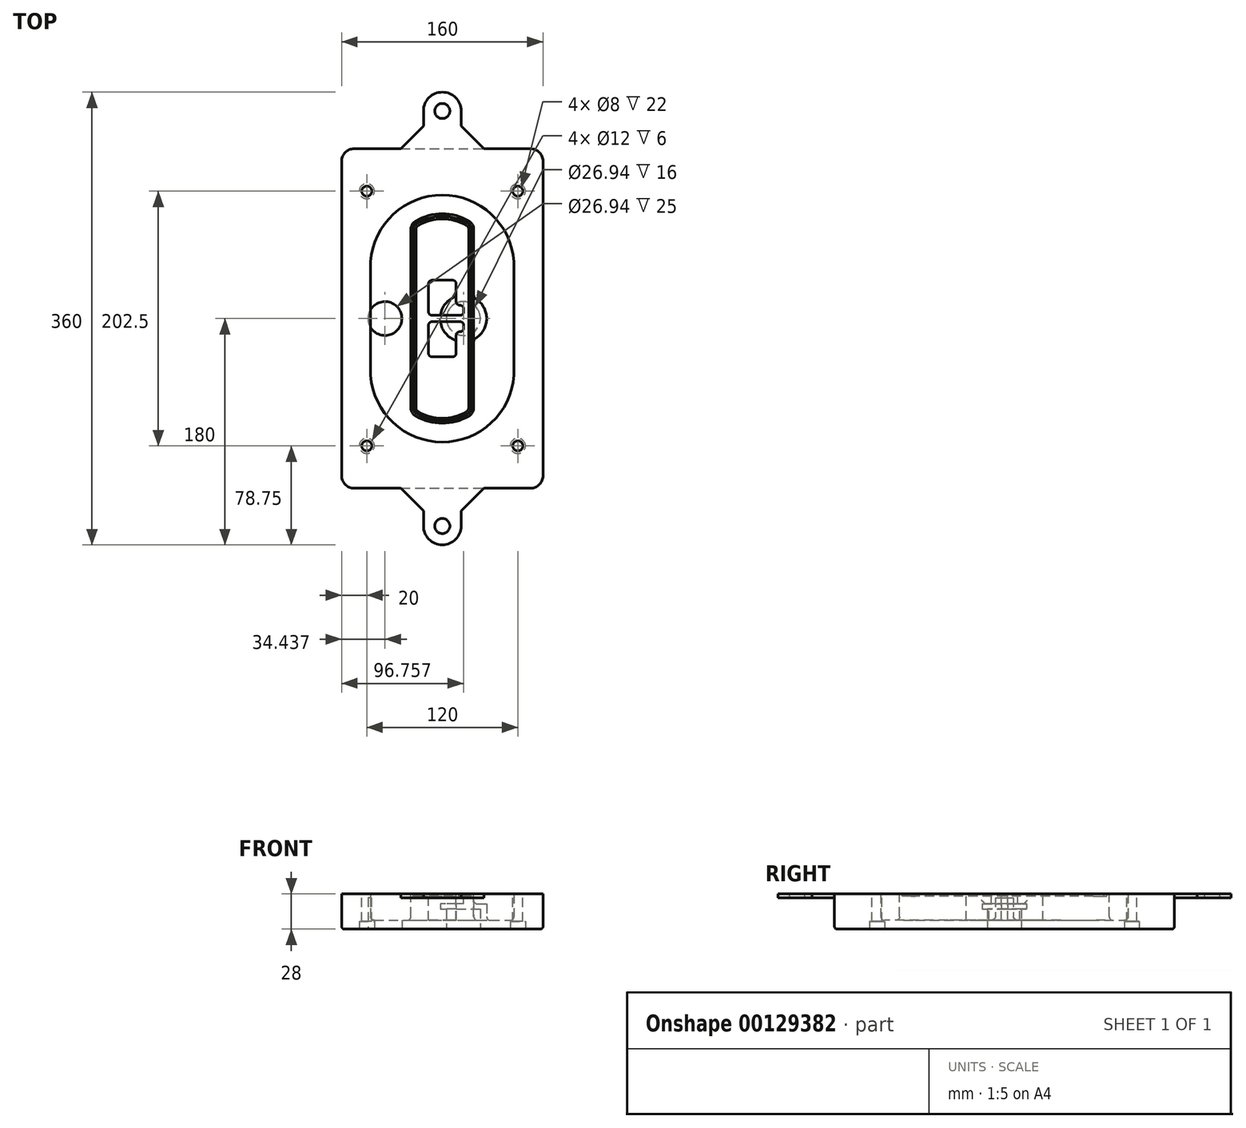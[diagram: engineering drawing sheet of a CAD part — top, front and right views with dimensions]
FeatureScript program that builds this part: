
annotation { "Feature Type Name" : "Feature", "Feature Type Description" : "" }
export const myFeature = defineFeature(function(context is Context, id is Id, definition is map)
    precondition{}
    {
        {
            var Q0;
            Q0=qCreatedBy(makeId("Top.planeOp"),FACE);
            var sketch = newSketch(context, id + "F0", { "sketchPlane" : qUnion([Q0])});
            skPoint(sketch, "E0.rect.middle", {"position": v(0, 0) * mm});
            skLineSegment(sketch, "E1.bottom", {"start": v(-70, -135) * mm, "end": v(70, -135) * mm});
            skLineSegment(sketch, "E1.top", {"start": v(-70, 135) * mm, "end": v(70, 135) * mm});
            skLineSegment(sketch, "E1.left", {"start": v(-80, -125) * mm, "end": v(-80, 125) * mm});
            skLineSegment(sketch, "E1.right", {"start": v(80, -125) * mm, "end": v(80, 125) * mm});
            skLineSegment(sketch, "E2", {"start": v(-80, 135) * mm, "end": v(80, -135) * mm, "construction": true});
            skLineSegment(sketch, "E3", {"start": v(80, 135) * mm, "end": v(-80, -135) * mm, "construction": true});
            skCircle(sketch, "E4", {"center": v(-60, 101.25) * mm, "radius": 4 * mm});
            skCircle(sketch, "E5", {"center": v(60, 101.25) * mm, "radius": 4 * mm});
            skCircle(sketch, "E6", {"center": v(60, -101.25) * mm, "radius": 4 * mm});
            skCircle(sketch, "E7", {"center": v(-60, -101.25) * mm, "radius": 4 * mm});
            skLineSegment(sketch, "E8", {"start": v(-60, 101.25) * mm, "end": v(60, 101.25) * mm, "construction": true});
            skLineSegment(sketch, "E9", {"start": v(60, 101.25) * mm, "end": v(60, -101.25) * mm, "construction": true});
            skLineSegment(sketch, "E10", {"start": v(60, -101.25) * mm, "end": v(-60, -101.25) * mm, "construction": true});
            skLineSegment(sketch, "E11", {"start": v(-60, -101.25) * mm, "end": v(-60, 101.25) * mm, "construction": true});
            skLineSegment(sketch, "E12", {"start": v(-60, 44.66) * mm, "end": v(-60, -44.66) * mm});
            skLineSegment(sketch, "E13", {"start": v(60, 44.66) * mm, "end": v(60, -44.66) * mm});
            skArc(sketch, "E14", {"start": v(59.98, 45.37) * mm, "mid": v(0, 101.25) * mm, "end": v(-59.98, 45.37) * mm});
            skArc(sketch, "E15", {"start": v(-59.98, -45.37) * mm, "mid": v(0, -101.25) * mm, "end": v(59.98, -45.37) * mm});
            skLineSegment(sketch, "E16", {"start": v(-60, 0) * mm, "end": v(60, 0) * mm, "construction": true});
            skPoint(sketch, "E17.visualSharp", {"position": v(-60, -45) * mm});
            skArc(sketch, "E17.filletArc", {"start": v(-60, -44.66) * mm, "mid": v(-60, -45.02) * mm, "end": v(-59.98, -45.37) * mm});
            skPoint(sketch, "E18.visualSharp", {"position": v(-60, 45) * mm});
            skArc(sketch, "E18.filletArc", {"start": v(-59.98, 45.37) * mm, "mid": v(-60, 45.02) * mm, "end": v(-60, 44.66) * mm});
            skPoint(sketch, "E19.visualSharp", {"position": v(60, 45) * mm});
            skArc(sketch, "E19.filletArc", {"start": v(60, 44.66) * mm, "mid": v(60, 45.02) * mm, "end": v(59.98, 45.37) * mm});
            skPoint(sketch, "E20.visualSharp", {"position": v(60, -45) * mm});
            skArc(sketch, "E20.filletArc", {"start": v(59.98, -45.37) * mm, "mid": v(60, -45.02) * mm, "end": v(60, -44.66) * mm});
            skPoint(sketch, "E21.visualSharp", {"position": v(-80, 135) * mm});
            skArc(sketch, "E21.filletArc", {"start": v(-70, 135) * mm, "mid": v(-77.07, 132.07) * mm, "end": v(-80, 125) * mm});
            skPoint(sketch, "E22.visualSharp", {"position": v(80, 135) * mm});
            skArc(sketch, "E22.filletArc", {"start": v(80, 125) * mm, "mid": v(77.07, 132.07) * mm, "end": v(70, 135) * mm});
            skPoint(sketch, "E23.visualSharp", {"position": v(80, -135) * mm});
            skArc(sketch, "E23.filletArc", {"start": v(70, -135) * mm, "mid": v(77.07, -132.07) * mm, "end": v(80, -125) * mm});
            skPoint(sketch, "E24.visualSharp", {"position": v(-80, -135) * mm});
            skArc(sketch, "E24.filletArc", {"start": v(-80, -125) * mm, "mid": v(-77.07, -132.07) * mm, "end": v(-70, -135) * mm});
            skArc(sketch, "E25.0", {"start": v(57, 44.66) * mm, "mid": v(57, 44.9) * mm, "end": v(56.98, 45.16) * mm});
            skLineSegment(sketch, "E25.1", {"start": v(57, 44.66) * mm, "end": v(57, -44.66) * mm});
            skArc(sketch, "E25.2", {"start": v(56.98, -45.16) * mm, "mid": v(57, -44.9) * mm, "end": v(57, -44.66) * mm});
            skArc(sketch, "E25.3", {"start": v(-56.98, -45.16) * mm, "mid": v(0, -98.25) * mm, "end": v(56.98, -45.16) * mm});
            skArc(sketch, "E25.4", {"start": v(-57, -44.66) * mm, "mid": v(-57, -44.9) * mm, "end": v(-56.98, -45.16) * mm});
            skArc(sketch, "E25.5", {"start": v(56.98, 45.16) * mm, "mid": v(0, 98.25) * mm, "end": v(-56.98, 45.16) * mm});
            skLineSegment(sketch, "E25.6", {"start": v(-57, 44.66) * mm, "end": v(-57, -44.66) * mm});
            skArc(sketch, "E25.7", {"start": v(-56.98, 45.16) * mm, "mid": v(-57, 44.9) * mm, "end": v(-57, 44.66) * mm});
            skArc(sketch, "E26.0", {"start": v(-63.97, 45.65) * mm, "mid": v(-64, 45.16) * mm, "end": v(-64, 44.66) * mm});
            skArc(sketch, "E26.1", {"start": v(63.97, 45.65) * mm, "mid": v(0, 105.25) * mm, "end": v(-63.97, 45.65) * mm});
            skArc(sketch, "E26.2", {"start": v(64, 44.66) * mm, "mid": v(64, 45.16) * mm, "end": v(63.97, 45.65) * mm});
            skLineSegment(sketch, "E26.3", {"start": v(64, 44.66) * mm, "end": v(64, -44.66) * mm});
            skArc(sketch, "E26.4", {"start": v(63.97, -45.65) * mm, "mid": v(64, -45.16) * mm, "end": v(64, -44.66) * mm});
            skLineSegment(sketch, "E26.5", {"start": v(-64, 44.66) * mm, "end": v(-64, -44.66) * mm});
            skArc(sketch, "E26.6", {"start": v(-63.97, -45.65) * mm, "mid": v(0, -105.25) * mm, "end": v(63.97, -45.65) * mm});
            skArc(sketch, "E26.7", {"start": v(-64, -44.66) * mm, "mid": v(-64, -45.16) * mm, "end": v(-63.97, -45.65) * mm});
            skSolve(sketch);
        }
        {
            var Q0;
            Q0=makeQuery(id+"F0.imprint","IMPRINT",FACE,{"disambiguationData":[TD([[makeQuery(id+"F0.imprint","IMPRINT",EDGE,{"derivedFrom":sQuery(id+"F0.wireOp",EDGE,"E1.bottom")}),1.0]])]});
            var Q1;
            Q1=makeQuery(id+"F0.imprint","IMPRINT",FACE,{"disambiguationData":[TD([[makeQuery(id+"F0.imprint","IMPRINT",EDGE,{"derivedFrom":sQuery(id+"F0.wireOp",EDGE,"E12")}),1.0]])]});
            var Q2;
            Q2=makeQuery(id+"F0.imprint","IMPRINT",FACE,{"disambiguationData":[TD([[makeQuery(id+"F0.imprint","IMPRINT",EDGE,{"derivedFrom":sQuery(id+"F0.wireOp",EDGE,"E25.0")}),1.0]])]});
            var Q3;
            Q3=makeQuery(id+"F0.imprint","IMPRINT",FACE,{"disambiguationData":[TD([[makeQuery(id+"F0.imprint","IMPRINT",EDGE,{"derivedFrom":sQuery(id+"F0.wireOp",EDGE,"E12")}),-1.0]])]});
            extrude(context, id + "F1", {"entities" : qUnion([Q0, Q1, Q2, Q3]), "oppositeDirection" : true, "depth" : 25 * mm});
        }
        {
            var Q0;
            Q0=makeQuery(id+"F0.imprint","IMPRINT",FACE,{"disambiguationData":[TD([[makeQuery(id+"F0.imprint","IMPRINT",EDGE,{"derivedFrom":sQuery(id+"F0.wireOp",EDGE,"E12")}),1.0]])]});
            extrude(context, id + "F2", {"entities" : qUnion([Q0]), "operationType" : NewBodyOperationType.ADD, "depth" : 3 * mm});
        }
        {
            var Q0;
            Q0=makeQuery(id+"F0.imprint","IMPRINT",FACE,{"disambiguationData":[TD([[makeQuery(id+"F0.imprint","IMPRINT",EDGE,{"derivedFrom":sQuery(id+"F0.wireOp",EDGE,"E25.0")}),1.0]])]});
            extrude(context, id + "F3", {"entities" : qUnion([Q0]), "operationType" : NewBodyOperationType.REMOVE, "oppositeDirection" : true, "depth" : 18 * mm});
        }
        {
            var Q0;
            Q0=makeQuery(id+"F2.opExtrude","CAP_FACE",FACE,{"disambiguationData":[OSD([sQuery(id+"F0.wireOp",EDGE,"E12"),sQuery(id+"F0.wireOp",EDGE,"E13"),sQuery(id+"F0.wireOp",EDGE,"E14"),sQuery(id+"F0.wireOp",EDGE,"E15"),sQuery(id+"F0.wireOp",EDGE,"E17.filletArc"),sQuery(id+"F0.wireOp",EDGE,"E18.filletArc"),sQuery(id+"F0.wireOp",EDGE,"E19.filletArc"),sQuery(id+"F0.wireOp",EDGE,"E20.filletArc"),sQuery(id+"F0.wireOp",EDGE,"E25.0"),sQuery(id+"F0.wireOp",EDGE,"E25.1"),sQuery(id+"F0.wireOp",EDGE,"E25.2"),sQuery(id+"F0.wireOp",EDGE,"E25.3"),sQuery(id+"F0.wireOp",EDGE,"E25.4"),sQuery(id+"F0.wireOp",EDGE,"E25.5"),sQuery(id+"F0.wireOp",EDGE,"E25.6"),sQuery(id+"F0.wireOp",EDGE,"E25.7")])],"isStart":false});
            var sketch = newSketch(context, id + "F4", { "sketchPlane" : qUnion([Q0])});
            skArc(sketch, "E27.0", {"start": v(-20.99, -77.65) * mm, "mid": v(0, -83.25) * mm, "end": v(20.99, -77.65) * mm});
            skArc(sketch, "E28.0", {"start": v(20.99, 77.65) * mm, "mid": v(0, 83.25) * mm, "end": v(-20.99, 77.65) * mm});
            skLineSegment(sketch, "E29", {"start": v(-25, 70.71) * mm, "end": v(-25, -70.71) * mm});
            skLineSegment(sketch, "E30", {"start": v(25, 70.71) * mm, "end": v(25, -70.71) * mm});
            skLineSegment(sketch, "E31", {"start": v(-25, 75.03) * mm, "end": v(25, 75.03) * mm, "construction": true});
            skLineSegment(sketch, "E32", {"start": v(-25, -75.03) * mm, "end": v(25, -75.03) * mm, "construction": true});
            skPoint(sketch, "E33.visualSharp", {"position": v(-25, 75.03) * mm});
            skArc(sketch, "E33.filletArc", {"start": v(-20.99, 77.65) * mm, "mid": v(-23.92, 74.72) * mm, "end": v(-25, 70.71) * mm});
            skPoint(sketch, "E34.visualSharp", {"position": v(25, 75.03) * mm});
            skArc(sketch, "E34.filletArc", {"start": v(25, 70.71) * mm, "mid": v(23.92, 74.72) * mm, "end": v(20.99, 77.65) * mm});
            skPoint(sketch, "E35.visualSharp", {"position": v(25, -75.03) * mm});
            skArc(sketch, "E35.filletArc", {"start": v(20.99, -77.65) * mm, "mid": v(23.92, -74.72) * mm, "end": v(25, -70.71) * mm});
            skPoint(sketch, "E36.visualSharp", {"position": v(-25, -75.03) * mm});
            skArc(sketch, "E36.filletArc", {"start": v(-25, -70.71) * mm, "mid": v(-23.92, -74.72) * mm, "end": v(-20.99, -77.65) * mm});
            skArc(sketch, "E37.0", {"start": v(56.98, 45.16) * mm, "mid": v(0, 98.25) * mm, "end": v(-56.98, 45.16) * mm});
            skArc(sketch, "E37.1", {"start": v(-56.98, 45.16) * mm, "mid": v(-57, 44.9) * mm, "end": v(-57, 44.66) * mm});
            skLineSegment(sketch, "E37.2", {"start": v(-57, 44.66) * mm, "end": v(-57, -44.66) * mm});
            skArc(sketch, "E37.3", {"start": v(-57, -44.66) * mm, "mid": v(-57, -44.9) * mm, "end": v(-56.98, -45.16) * mm});
            skArc(sketch, "E37.4", {"start": v(-56.98, -45.16) * mm, "mid": v(0, -98.25) * mm, "end": v(56.98, -45.16) * mm});
            skArc(sketch, "E37.5", {"start": v(56.98, -45.16) * mm, "mid": v(57, -44.9) * mm, "end": v(57, -44.66) * mm});
            skLineSegment(sketch, "E37.6", {"start": v(57, 44.66) * mm, "end": v(57, -44.66) * mm});
            skArc(sketch, "E37.7", {"start": v(57, 44.66) * mm, "mid": v(57, 44.9) * mm, "end": v(56.98, 45.16) * mm});
            skLineSegment(sketch, "E38.0", {"start": v(23, 70.71) * mm, "end": v(23, -70.71) * mm});
            skArc(sketch, "E38.1", {"start": v(19.99, -75.92) * mm, "mid": v(22.2, -73.72) * mm, "end": v(23, -70.71) * mm});
            skArc(sketch, "E38.2", {"start": v(-19.99, -75.92) * mm, "mid": v(0, -81.25) * mm, "end": v(19.99, -75.92) * mm});
            skArc(sketch, "E38.3", {"start": v(-23, -70.71) * mm, "mid": v(-22.2, -73.72) * mm, "end": v(-19.99, -75.92) * mm});
            skLineSegment(sketch, "E38.4", {"start": v(-23, 70.71) * mm, "end": v(-23, -70.71) * mm});
            skArc(sketch, "E38.5", {"start": v(23, 70.71) * mm, "mid": v(22.2, 73.72) * mm, "end": v(19.99, 75.92) * mm});
            skArc(sketch, "E38.6", {"start": v(-19.99, 75.92) * mm, "mid": v(-22.2, 73.72) * mm, "end": v(-23, 70.71) * mm});
            skArc(sketch, "E38.7", {"start": v(19.99, 75.92) * mm, "mid": v(0, 81.25) * mm, "end": v(-19.99, 75.92) * mm});
            skArc(sketch, "E39.0", {"start": v(21, 70.71) * mm, "mid": v(20.46, 72.72) * mm, "end": v(19, 74.18) * mm});
            skLineSegment(sketch, "E39.1", {"start": v(21, 70.71) * mm, "end": v(21, -70.71) * mm});
            skArc(sketch, "E39.2", {"start": v(19, -74.18) * mm, "mid": v(20.46, -72.72) * mm, "end": v(21, -70.71) * mm});
            skArc(sketch, "E39.3", {"start": v(-19, -74.18) * mm, "mid": v(0, -79.25) * mm, "end": v(19, -74.18) * mm});
            skArc(sketch, "E39.4", {"start": v(-21, -70.71) * mm, "mid": v(-20.46, -72.72) * mm, "end": v(-19, -74.18) * mm});
            skArc(sketch, "E39.5", {"start": v(19, 74.18) * mm, "mid": v(0, 79.25) * mm, "end": v(-19, 74.18) * mm});
            skLineSegment(sketch, "E39.6", {"start": v(-21, 70.71) * mm, "end": v(-21, -70.71) * mm});
            skArc(sketch, "E39.7", {"start": v(-19, 74.18) * mm, "mid": v(-20.46, 72.72) * mm, "end": v(-21, 70.71) * mm});
            skLineSegment(sketch, "E40", {"start": v(-25, 0) * mm, "end": v(25, 0) * mm, "construction": true});
            skLineSegment(sketch, "E41", {"start": v(-11, 5.5) * mm, "end": v(-11, 27.5) * mm});
            skLineSegment(sketch, "E42", {"start": v(-8, 30.5) * mm, "end": v(8, 30.5) * mm});
            skLineSegment(sketch, "E43", {"start": v(11, 27.5) * mm, "end": v(11, 13.5) * mm});
            skLineSegment(sketch, "E44", {"start": v(14, 10.5) * mm, "end": v(14, 10.5) * mm});
            skLineSegment(sketch, "E45", {"start": v(17, 7.5) * mm, "end": v(17, 5.5) * mm});
            skLineSegment(sketch, "E46", {"start": v(14, 2.5) * mm, "end": v(-8, 2.5) * mm});
            skPoint(sketch, "E47.visualSharp", {"position": v(-11, 30.5) * mm});
            skArc(sketch, "E47.filletArc", {"start": v(-8, 30.5) * mm, "mid": v(-10.12, 29.62) * mm, "end": v(-11, 27.5) * mm});
            skPoint(sketch, "E48.visualSharp", {"position": v(11, 30.5) * mm});
            skArc(sketch, "E48.filletArc", {"start": v(11, 27.5) * mm, "mid": v(10.12, 29.62) * mm, "end": v(8, 30.5) * mm});
            skPoint(sketch, "E49.visualSharp", {"position": v(11, 10.5) * mm});
            skArc(sketch, "E49.filletArc", {"start": v(11, 13.5) * mm, "mid": v(11.88, 11.38) * mm, "end": v(14, 10.5) * mm});
            skPoint(sketch, "E50.visualSharp", {"position": v(17, 10.5) * mm});
            skArc(sketch, "E50.filletArc", {"start": v(17, 7.5) * mm, "mid": v(16.12, 9.62) * mm, "end": v(14, 10.5) * mm});
            skPoint(sketch, "E51.visualSharp", {"position": v(17, 2.5) * mm});
            skArc(sketch, "E51.filletArc", {"start": v(14, 2.5) * mm, "mid": v(16.12, 3.38) * mm, "end": v(17, 5.5) * mm});
            skPoint(sketch, "E52.visualSharp", {"position": v(-11, 2.5) * mm});
            skArc(sketch, "E52.filletArc", {"start": v(-11, 5.5) * mm, "mid": v(-10.12, 3.38) * mm, "end": v(-8, 2.5) * mm});
            skLineSegment(sketch, "E53.0.MirrorCS", {"start": v(14, -2.5) * mm, "end": v(-8, -2.5) * mm});
            skArc(sketch, "E54.0.MirrorCS", {"start": v(-11, -5.5) * mm, "mid": v(-10.12, -3.38) * mm, "end": v(-8, -2.5) * mm});
            skLineSegment(sketch, "E55.0.MirrorCS", {"start": v(-11, -5.5) * mm, "end": v(-11, -27.5) * mm});
            skArc(sketch, "E56.0.MirrorCS", {"start": v(-8, -30.5) * mm, "mid": v(-10.12, -29.62) * mm, "end": v(-11, -27.5) * mm});
            skLineSegment(sketch, "E57.0.MirrorCS", {"start": v(-8, -30.5) * mm, "end": v(8, -30.5) * mm});
            skArc(sketch, "E58.0.MirrorCS", {"start": v(11, -27.5) * mm, "mid": v(10.12, -29.62) * mm, "end": v(8, -30.5) * mm});
            skLineSegment(sketch, "E59.0.MirrorCS", {"start": v(11, -27.5) * mm, "end": v(11, -13.5) * mm});
            skArc(sketch, "E60.0.MirrorCS", {"start": v(11, -13.5) * mm, "mid": v(11.88, -11.38) * mm, "end": v(14, -10.5) * mm});
            skArc(sketch, "E61.0.MirrorCS", {"start": v(17, -7.5) * mm, "mid": v(16.12, -9.62) * mm, "end": v(14, -10.5) * mm});
            skLineSegment(sketch, "E62.0.MirrorCS", {"start": v(17, -7.5) * mm, "end": v(17, -5.5) * mm});
            skArc(sketch, "E63.0.MirrorCS", {"start": v(14, -2.5) * mm, "mid": v(16.12, -3.38) * mm, "end": v(17, -5.5) * mm});
            skSolve(sketch);
        }
        {
            var Q0;
            Q0=makeQuery(id+"F4.imprint","IMPRINT",FACE,{"disambiguationData":[TD([[makeQuery(id+"F4.imprint","IMPRINT",EDGE,{"derivedFrom":sQuery(id+"F4.wireOp",EDGE,"E27.0")}),1.0]])]});
            var Q1;
            Q1=makeQuery(id+"F4.imprint","IMPRINT",FACE,{"disambiguationData":[TD([[makeQuery(id+"F4.imprint","IMPRINT",EDGE,{"derivedFrom":sQuery(id+"F4.wireOp",EDGE,"E38.0")}),-1.0]])]});
            var Q2;
            Q2=makeQuery(id+"F4.imprint","IMPRINT",FACE,{"disambiguationData":[TD([[makeQuery(id+"F4.imprint","IMPRINT",EDGE,{"derivedFrom":sQuery(id+"F4.wireOp",EDGE,"E39.0")}),1.0]])]});
            extrude(context, id + "F5", {"entities" : qUnion([Q0, Q1, Q2]), "operationType" : NewBodyOperationType.ADD, "endBound" : BoundingType.UP_TO_NEXT, "oppositeDirection" : true, "depth" : 25 * mm});
        }
        {
            var Q0;
            Q0=makeQuery(id+"F4.imprint","IMPRINT",FACE,{"disambiguationData":[TD([[makeQuery(id+"F4.imprint","IMPRINT",EDGE,{"derivedFrom":sQuery(id+"F4.wireOp",EDGE,"E38.0")}),-1.0]])]});
            extrude(context, id + "F6", {"entities" : qUnion([Q0]), "operationType" : NewBodyOperationType.REMOVE, "oppositeDirection" : true, "depth" : 2 * mm});
        }
        {
            var Q0;
            Q0=makeQuery(id+"F1.opExtrude","CAP_FACE",FACE,{"disambiguationData":[OSD([sQuery(id+"F0.wireOp",EDGE,"E1.bottom"),sQuery(id+"F0.wireOp",EDGE,"E1.top"),sQuery(id+"F0.wireOp",EDGE,"E1.left"),sQuery(id+"F0.wireOp",EDGE,"E1.right"),sQuery(id+"F0.wireOp",EDGE,"E4"),sQuery(id+"F0.wireOp",EDGE,"E5"),sQuery(id+"F0.wireOp",EDGE,"E6"),sQuery(id+"F0.wireOp",EDGE,"E7"),sQuery(id+"F0.wireOp",EDGE,"E21.filletArc"),sQuery(id+"F0.wireOp",EDGE,"E22.filletArc"),sQuery(id+"F0.wireOp",EDGE,"E23.filletArc"),sQuery(id+"F0.wireOp",EDGE,"E24.filletArc")])],"isStart":false});
            var sketch = newSketch(context, id + "F7", { "sketchPlane" : qUnion([Q0])});
            skCircle(sketch, "E64", {"center": v(16.76, 0) * mm, "radius": 13.47 * mm});
            skCircle(sketch, "E65", {"center": v(-45.56, 0) * mm, "radius": 13.47 * mm});
            skLineSegment(sketch, "E66", {"start": v(80, 0) * mm, "end": v(-80, 0) * mm});
            skCircle(sketch, "E67", {"center": v(16.76, 0) * mm, "radius": 18.47 * mm});
            skCircle(sketch, "E68", {"center": v(60, -101.25) * mm, "radius": 6 * mm});
            skCircle(sketch, "E69", {"center": v(-60, -101.25) * mm, "radius": 6 * mm});
            skCircle(sketch, "E70", {"center": v(-60, 101.25) * mm, "radius": 6 * mm});
            skCircle(sketch, "E71", {"center": v(60, 101.25) * mm, "radius": 6 * mm});
            skSolve(sketch);
        }
        {
            var Q0;
            {var subQ1=sQuery(id+"F7.wireOp",EDGE,"E66");var subQ4=sQuery(id+"F7.wireOp",EDGE,"E64");var subQ6=makeQuery(id+"F7.imprint","INTERSECT",VERTEX,{"disambiguationData":[OD(0.0)],"derivedFrom":[subQ4,subQ1]});Q0=makeQuery(id+"F7.imprint","IMPRINT",FACE,{"disambiguationData":[TD([[makeQuery(id+"F7.imprint","IMPRINT",EDGE,{"disambiguationData":[TD([[subQ6,-1.0]])],"derivedFrom":subQ4}),-1.0]])]});}
            var Q1;
            {var subQ0=sQuery(id+"F7.wireOp",EDGE,"E66");var subQ1=sQuery(id+"F7.wireOp",EDGE,"E64");var subQ3=makeQuery(id+"F7.imprint","INTERSECT",VERTEX,{"disambiguationData":[OD(0.0)],"derivedFrom":[subQ1,subQ0]});Q1=makeQuery(id+"F7.imprint","IMPRINT",FACE,{"disambiguationData":[TD([[makeQuery(id+"F7.imprint","IMPRINT",EDGE,{"disambiguationData":[TD([[subQ3,-1.0]])],"derivedFrom":subQ1}),1.0]])]});}
            var Q2;
            {var subQ0=sQuery(id+"F7.wireOp",EDGE,"E66");var subQ1=sQuery(id+"F7.wireOp",EDGE,"E64");var subQ3=makeQuery(id+"F7.imprint","INTERSECT",VERTEX,{"disambiguationData":[OD(0.0)],"derivedFrom":[subQ1,subQ0]});Q2=makeQuery(id+"F7.imprint","IMPRINT",FACE,{"disambiguationData":[TD([[makeQuery(id+"F7.imprint","IMPRINT",EDGE,{"disambiguationData":[TD([[subQ3,1.0]])],"derivedFrom":subQ1}),1.0]])]});}
            var Q3;
            {var subQ1=sQuery(id+"F7.wireOp",EDGE,"E66");var subQ4=sQuery(id+"F7.wireOp",EDGE,"E64");var subQ6=makeQuery(id+"F7.imprint","INTERSECT",VERTEX,{"disambiguationData":[OD(0.0)],"derivedFrom":[subQ4,subQ1]});Q3=makeQuery(id+"F7.imprint","IMPRINT",FACE,{"disambiguationData":[TD([[makeQuery(id+"F7.imprint","IMPRINT",EDGE,{"disambiguationData":[TD([[subQ6,1.0]])],"derivedFrom":subQ4}),-1.0]])]});}
            extrude(context, id + "F8", {"entities" : qUnion([Q0, Q1, Q2, Q3]), "operationType" : NewBodyOperationType.ADD, "oppositeDirection" : true, "depth" : 20 * mm});
        }
        {
            var Q0;
            {var subQ0=sQuery(id+"F7.wireOp",EDGE,"E66");var subQ1=sQuery(id+"F7.wireOp",EDGE,"E64");var subQ3=makeQuery(id+"F7.imprint","INTERSECT",VERTEX,{"disambiguationData":[OD(0.0)],"derivedFrom":[subQ1,subQ0]});Q0=makeQuery(id+"F7.imprint","IMPRINT",FACE,{"disambiguationData":[TD([[makeQuery(id+"F7.imprint","IMPRINT",EDGE,{"disambiguationData":[TD([[subQ3,-1.0]])],"derivedFrom":subQ1}),1.0]])]});}
            var Q1;
            {var subQ0=sQuery(id+"F7.wireOp",EDGE,"E66");var subQ1=sQuery(id+"F7.wireOp",EDGE,"E64");var subQ3=makeQuery(id+"F7.imprint","INTERSECT",VERTEX,{"disambiguationData":[OD(0.0)],"derivedFrom":[subQ1,subQ0]});Q1=makeQuery(id+"F7.imprint","IMPRINT",FACE,{"disambiguationData":[TD([[makeQuery(id+"F7.imprint","IMPRINT",EDGE,{"disambiguationData":[TD([[subQ3,1.0]])],"derivedFrom":subQ1}),1.0]])]});}
            extrude(context, id + "F9", {"entities" : qUnion([Q0, Q1]), "operationType" : NewBodyOperationType.REMOVE, "oppositeDirection" : true, "depth" : 16 * mm});
        }
        {
            var Q0;
            {var subQ0=sQuery(id+"F7.wireOp",EDGE,"E66");var subQ1=sQuery(id+"F7.wireOp",EDGE,"E65");var subQ3=makeQuery(id+"F7.imprint","INTERSECT",VERTEX,{"disambiguationData":[OD(0.0)],"derivedFrom":[subQ1,subQ0]});Q0=makeQuery(id+"F7.imprint","IMPRINT",FACE,{"disambiguationData":[TD([[makeQuery(id+"F7.imprint","IMPRINT",EDGE,{"disambiguationData":[TD([[subQ3,-1.0]])],"derivedFrom":subQ1}),1.0]])]});}
            var Q1;
            {var subQ0=sQuery(id+"F7.wireOp",EDGE,"E66");var subQ1=sQuery(id+"F7.wireOp",EDGE,"E65");var subQ3=makeQuery(id+"F7.imprint","INTERSECT",VERTEX,{"disambiguationData":[OD(0.0)],"derivedFrom":[subQ1,subQ0]});Q1=makeQuery(id+"F7.imprint","IMPRINT",FACE,{"disambiguationData":[TD([[makeQuery(id+"F7.imprint","IMPRINT",EDGE,{"disambiguationData":[TD([[subQ3,1.0]])],"derivedFrom":subQ1}),1.0]])]});}
            extrude(context, id + "F10", {"entities" : qUnion([Q0, Q1]), "operationType" : NewBodyOperationType.REMOVE, "oppositeDirection" : true, "depth" : 25 * mm});
        }
        {
            var Q0;
            Q0=makeQuery(id+"F7.imprint","IMPRINT",FACE,{"disambiguationData":[TD([[makeQuery(id+"F7.imprint","IMPRINT",EDGE,{"derivedFrom":sQuery(id+"F7.wireOp",EDGE,"E68")}),1.0]])]});
            var Q1;
            Q1=makeQuery(id+"F7.imprint","IMPRINT",FACE,{"disambiguationData":[TD([[makeQuery(id+"F7.imprint","IMPRINT",EDGE,{"derivedFrom":makeQuery(id+"F1.opExtrude","CAP_EDGE",EDGE,{"disambiguationData":[OSD([sQuery(id+"F0.wireOp",EDGE,"E5")])],"isStart":false})}),-1.0]])]});
            var Q2;
            Q2=makeQuery(id+"F7.imprint","IMPRINT",FACE,{"disambiguationData":[TD([[makeQuery(id+"F7.imprint","IMPRINT",EDGE,{"derivedFrom":sQuery(id+"F7.wireOp",EDGE,"E69")}),1.0]])]});
            var Q3;
            Q3=makeQuery(id+"F7.imprint","IMPRINT",FACE,{"disambiguationData":[TD([[makeQuery(id+"F7.imprint","IMPRINT",EDGE,{"derivedFrom":makeQuery(id+"F1.opExtrude","CAP_EDGE",EDGE,{"disambiguationData":[OSD([sQuery(id+"F0.wireOp",EDGE,"E4")])],"isStart":false})}),-1.0]])]});
            var Q4;
            Q4=makeQuery(id+"F7.imprint","IMPRINT",FACE,{"disambiguationData":[TD([[makeQuery(id+"F7.imprint","IMPRINT",EDGE,{"derivedFrom":sQuery(id+"F7.wireOp",EDGE,"E70")}),1.0]])]});
            var Q5;
            Q5=makeQuery(id+"F7.imprint","IMPRINT",FACE,{"disambiguationData":[TD([[makeQuery(id+"F7.imprint","IMPRINT",EDGE,{"derivedFrom":makeQuery(id+"F1.opExtrude","CAP_EDGE",EDGE,{"disambiguationData":[OSD([sQuery(id+"F0.wireOp",EDGE,"E7")])],"isStart":false})}),-1.0]])]});
            var Q6;
            Q6=makeQuery(id+"F7.imprint","IMPRINT",FACE,{"disambiguationData":[TD([[makeQuery(id+"F7.imprint","IMPRINT",EDGE,{"derivedFrom":sQuery(id+"F7.wireOp",EDGE,"E71")}),1.0]])]});
            var Q7;
            Q7=makeQuery(id+"F7.imprint","IMPRINT",FACE,{"disambiguationData":[TD([[makeQuery(id+"F7.imprint","IMPRINT",EDGE,{"derivedFrom":makeQuery(id+"F1.opExtrude","CAP_EDGE",EDGE,{"disambiguationData":[OSD([sQuery(id+"F0.wireOp",EDGE,"E6")])],"isStart":false})}),-1.0]])]});
            extrude(context, id + "F11", {"entities" : qUnion([Q0, Q1, Q2, Q3, Q4, Q5, Q6, Q7]), "operationType" : NewBodyOperationType.REMOVE, "oppositeDirection" : true, "depth" : 6 * mm});
        }
        {
            var Q0;
            Q0=makeQuery(id+"F9.boolean.opBoolean","COPY",FACE,{"derivedFrom":makeQuery(id+"F9.opExtrude","CAP_FACE",FACE,{"disambiguationData":[OSD([sQuery(id+"F7.wireOp",EDGE,"E64")])],"isStart":false})});
            var sketch = newSketch(context, id + "F12", { "sketchPlane" : qUnion([Q0])});
            skArc(sketch, "E72.0", {"start": v(11, 17.55) * mm, "mid": v(2.57, 11.82) * mm, "end": v(-1.54, 2.5) * mm});
            skArc(sketch, "E72.1", {"start": v(-1.54, -2.5) * mm, "mid": v(2.57, -11.82) * mm, "end": v(11, -17.55) * mm});
            skLineSegment(sketch, "E73", {"start": v(-1.54, -2.5) * mm, "end": v(14, -2.5) * mm});
            skLineSegment(sketch, "E74.0", {"start": v(14, 2.5) * mm, "end": v(-1.54, 2.5) * mm});
            skArc(sketch, "E74.1", {"start": v(14, 2.5) * mm, "mid": v(16.12, 3.38) * mm, "end": v(17, 5.5) * mm});
            skLineSegment(sketch, "E74.2", {"start": v(17, 7.5) * mm, "end": v(17, 5.5) * mm});
            skArc(sketch, "E74.3", {"start": v(17, 7.5) * mm, "mid": v(16.12, 9.62) * mm, "end": v(14, 10.5) * mm});
            skArc(sketch, "E74.4", {"start": v(11, 13.5) * mm, "mid": v(11.88, 11.38) * mm, "end": v(14, 10.5) * mm});
            skLineSegment(sketch, "E74.5", {"start": v(11, 17.55) * mm, "end": v(11, 13.5) * mm});
            skLineSegment(sketch, "E74.7", {"start": v(14, -2.5) * mm, "end": v(-1.54, -2.5) * mm});
            skArc(sketch, "E74.8", {"start": v(14, -2.5) * mm, "mid": v(16.12, -3.38) * mm, "end": v(17, -5.5) * mm});
            skLineSegment(sketch, "E74.9", {"start": v(17, -7.5) * mm, "end": v(17, -5.5) * mm});
            skArc(sketch, "E74.10", {"start": v(17, -7.5) * mm, "mid": v(16.12, -9.62) * mm, "end": v(14, -10.5) * mm});
            skArc(sketch, "E74.11", {"start": v(11, -13.5) * mm, "mid": v(11.88, -11.38) * mm, "end": v(14, -10.5) * mm});
            skLineSegment(sketch, "E74.12", {"start": v(11, -17.55) * mm, "end": v(11, -13.5) * mm});
            skPoint(sketch, "E75.orphan", {"position": v(11, -27.5) * mm});
            skPoint(sketch, "E76.orphan", {"position": v(-8, -2.5) * mm});
            skPoint(sketch, "E77.orphan", {"position": v(-8, 2.5) * mm});
            skPoint(sketch, "E78.orphan", {"position": v(11, 27.5) * mm});
            skSolve(sketch);
        }
        {
            var Q0;
            {var subQ7=sQuery(id+"F12.wireOp",EDGE,"E72.0");var subQ14=sQuery(id+"F12.wireOp",EDGE,"E72.1");var subQ16=sQuery(id+"F12.wireOp",EDGE,"E74.1");var subQ18=sQuery(id+"F12.wireOp",EDGE,"E74.8");Q0=qUnion([makeQuery(id+"F12.imprint","IMPRINT",FACE,{"disambiguationData":[TD([[makeQuery(id+"F12.imprint","IMPRINT",EDGE,{"derivedFrom":subQ7}),1.0]])]}),makeQuery(id+"F12.imprint","IMPRINT",FACE,{"disambiguationData":[TD([[makeQuery(id+"F12.imprint","IMPRINT",EDGE,{"derivedFrom":subQ14}),1.0]])]}),makeQuery(id+"F12.imprint","IMPRINT",FACE,{"disambiguationData":[TD([[makeQuery(id+"F12.imprint","IMPRINT",EDGE,{"derivedFrom":subQ16}),1.0]])]}),makeQuery(id+"F12.imprint","IMPRINT",FACE,{"disambiguationData":[TD([[makeQuery(id+"F12.imprint","IMPRINT",EDGE,{"derivedFrom":subQ18}),-1.0]])]})]);}
            var Q1;
            Q1=makeQuery(id+"F5.boolean.opBoolean","SPLIT",FACE,{"disambiguationData":[TD([makeQuery(id+"F5.opExtrude","SWEPT_FACE",FACE,{"disambiguationData":[OSD([sQuery(id+"F4.wireOp",EDGE,"E41")])]})])],"derivedFrom":makeQuery(id+"F3.boolean.opBoolean","COPY",FACE,{"derivedFrom":makeQuery(id+"F3.opExtrude","CAP_FACE",FACE,{"disambiguationData":[OSD([sQuery(id+"F0.wireOp",EDGE,"E25.0"),sQuery(id+"F0.wireOp",EDGE,"E25.1"),sQuery(id+"F0.wireOp",EDGE,"E25.2"),sQuery(id+"F0.wireOp",EDGE,"E25.3"),sQuery(id+"F0.wireOp",EDGE,"E25.4"),sQuery(id+"F0.wireOp",EDGE,"E25.5"),sQuery(id+"F0.wireOp",EDGE,"E25.6"),sQuery(id+"F0.wireOp",EDGE,"E25.7")])],"isStart":false})})});
            extrude(context, id + "F13", {"entities" : qUnion([Q0]), "operationType" : NewBodyOperationType.REMOVE, "endBound" : BoundingType.UP_TO_SURFACE, "endBoundEntityFace" : qUnion([Q1]), "depth" : 25 * mm});
        }
        {
            var Q0;
            Q0=makeQuery(id+"F3.boolean.opBoolean","COPY",EDGE,{"derivedFrom":makeQuery(id+"F3.opExtrude","CAP_EDGE",EDGE,{"disambiguationData":[OSD([sQuery(id+"F0.wireOp",EDGE,"E25.6")])],"isStart":false})});
            var Q1;
            Q1=makeQuery(id+"F8.boolean.opBoolean","INTERSECT",EDGE,{"derivedFrom":[makeQuery(id+"F5.opExtrude","SWEPT_FACE",FACE,{"disambiguationData":[OSD([sQuery(id+"F4.wireOp",EDGE,"E30")])]}),makeQuery(id+"F8.opExtrude","CAP_FACE",FACE,{"disambiguationData":[OSD([sQuery(id+"F7.wireOp",EDGE,"E67")])],"isStart":false})]});
            var Q2;
            Q2=makeQuery(id+"F8.boolean.opBoolean","INTERSECT",EDGE,{"disambiguationData":[OD(1.0)],"derivedFrom":[makeQuery(id+"F5.opExtrude","SWEPT_FACE",FACE,{"disambiguationData":[OSD([sQuery(id+"F4.wireOp",EDGE,"E30")])]}),makeQuery(id+"F8.opExtrude","SWEPT_FACE",FACE,{"disambiguationData":[OSD([sQuery(id+"F7.wireOp",EDGE,"E67")])]})]});
            var Q3;
            {var subQ0=sQuery(id+"F4.wireOp",EDGE,"E30");Q3=makeQuery(id+"F8.boolean.opBoolean","SPLIT",EDGE,{"disambiguationData":[TD([makeQuery(id+"F5.opExtrude","SWEPT_FACE",FACE,{"disambiguationData":[OSD([sQuery(id+"F4.wireOp",EDGE,"E35.filletArc")])]})])],"derivedFrom":makeQuery(id+"F5.opExtrude","CAP_EDGE",EDGE,{"disambiguationData":[OSD([subQ0])],"isStart":false})});}
            var Q4;
            {var subQ0=sQuery(id+"F0.wireOp",EDGE,"E25.7");var subQ1=sQuery(id+"F0.wireOp",EDGE,"E25.1");var subQ2=sQuery(id+"F0.wireOp",EDGE,"E25.6");var subQ3=sQuery(id+"F0.wireOp",EDGE,"E25.5");var subQ4=sQuery(id+"F0.wireOp",EDGE,"E25.4");var subQ5=sQuery(id+"F0.wireOp",EDGE,"E25.0");var subQ6=sQuery(id+"F0.wireOp",EDGE,"E25.2");var subQ7=sQuery(id+"F0.wireOp",EDGE,"E25.3");Q4=makeQuery(id+"F8.boolean.opBoolean","INTERSECT",EDGE,{"derivedFrom":[makeQuery(id+"F5.boolean.opBoolean","SPLIT",FACE,{"disambiguationData":[TD([makeQuery(id+"F2.opExtrude","SWEPT_FACE",FACE,{"disambiguationData":[OSD([subQ5])]})])],"derivedFrom":makeQuery(id+"F3.boolean.opBoolean","COPY",FACE,{"derivedFrom":makeQuery(id+"F3.opExtrude","CAP_FACE",FACE,{"disambiguationData":[OSD([subQ5,subQ1,subQ6,subQ7,subQ4,subQ3,subQ2,subQ0])],"isStart":false})})}),makeQuery(id+"F8.opExtrude","SWEPT_FACE",FACE,{"disambiguationData":[OSD([sQuery(id+"F7.wireOp",EDGE,"E67")])]})]});}
            var Q5;
            Q5=makeQuery(id+"F8.boolean.opBoolean","INTERSECT",EDGE,{"disambiguationData":[OD(0.0)],"derivedFrom":[makeQuery(id+"F5.opExtrude","SWEPT_FACE",FACE,{"disambiguationData":[OSD([sQuery(id+"F4.wireOp",EDGE,"E30")])]}),makeQuery(id+"F8.opExtrude","SWEPT_FACE",FACE,{"disambiguationData":[OSD([sQuery(id+"F7.wireOp",EDGE,"E67")])]})]});
            fillet(context, id + "F14", {"entities" : qUnion([Q0, Q1, Q2, Q3, Q4, Q5]), "radius" : 3 * mm, "tangentPropagation" : true, "allowEdgeOverflow" : false});
        }
        {
            var Q0;
            Q0=makeQuery(id+"F1.opExtrude","CAP_EDGE",EDGE,{"disambiguationData":[OSD([sQuery(id+"F0.wireOp",EDGE,"E1.bottom")])],"isStart":false});
            fillet(context, id + "F15", {"entities" : qUnion([Q0]), "radius" : 2 * mm, "tangentPropagation" : true, "allowEdgeOverflow" : false});
        }
        {
            var Q0;
            {var subQ0=sQuery(id+"F0.wireOp",EDGE,"E22.filletArc");var subQ1=sQuery(id+"F0.wireOp",EDGE,"E7");var subQ2=sQuery(id+"F0.wireOp",EDGE,"E6");var subQ3=sQuery(id+"F0.wireOp",EDGE,"E5");var subQ4=sQuery(id+"F0.wireOp",EDGE,"E4");var subQ5=sQuery(id+"F0.wireOp",EDGE,"E1.bottom");var subQ6=sQuery(id+"F0.wireOp",EDGE,"E21.filletArc");var subQ7=sQuery(id+"F0.wireOp",EDGE,"E1.top");var subQ8=sQuery(id+"F0.wireOp",EDGE,"E1.left");var subQ9=sQuery(id+"F0.wireOp",EDGE,"E1.right");var subQ10=sQuery(id+"F0.wireOp",EDGE,"E23.filletArc");var subQ11=sQuery(id+"F0.wireOp",EDGE,"E24.filletArc");Q0=makeQuery(id+"F2.boolean.opBoolean","SPLIT",FACE,{"disambiguationData":[TD([makeQuery(id+"F1.opExtrude","SWEPT_FACE",FACE,{"disambiguationData":[OSD([subQ5])]})])],"derivedFrom":makeQuery(id+"F1.opExtrude","CAP_FACE",FACE,{"disambiguationData":[OSD([subQ5,subQ7,subQ8,subQ9,subQ4,subQ3,subQ2,subQ1,subQ6,subQ0,subQ10,subQ11])],"isStart":true})});}
            var sketch = newSketch(context, id + "F16", { "sketchPlane" : qUnion([Q0])});
            skArc(sketch, "E79.0", {"start": v(70, -135) * mm, "mid": v(77.07, -132.07) * mm, "end": v(80, -125) * mm});
            skLineSegment(sketch, "E79.1", {"start": v(80, -125) * mm, "end": v(80, 125) * mm});
            skArc(sketch, "E79.2", {"start": v(80, 125) * mm, "mid": v(77.07, 132.07) * mm, "end": v(70, 135) * mm});
            skLineSegment(sketch, "E79.3", {"start": v(-70, 135) * mm, "end": v(70, 135) * mm});
            skArc(sketch, "E79.4", {"start": v(-70, 135) * mm, "mid": v(-77.07, 132.07) * mm, "end": v(-80, 125) * mm});
            skLineSegment(sketch, "E79.5", {"start": v(-80, -125) * mm, "end": v(-80, 125) * mm});
            skArc(sketch, "E79.6", {"start": v(-80, -125) * mm, "mid": v(-77.07, -132.07) * mm, "end": v(-70, -135) * mm});
            skLineSegment(sketch, "E79.7", {"start": v(-70, -135) * mm, "end": v(70, -135) * mm});
            skCircle(sketch, "E79.8", {"center": v(-60, -101.25) * mm, "radius": 4 * mm});
            skCircle(sketch, "E79.9", {"center": v(60, -101.25) * mm, "radius": 4 * mm});
            skCircle(sketch, "E79.10", {"center": v(60, 101.25) * mm, "radius": 4 * mm});
            skCircle(sketch, "E79.11", {"center": v(-60, 101.25) * mm, "radius": 4 * mm});
            skLineSegment(sketch, "E79.12", {"start": v(-60, 44.66) * mm, "end": v(-60, -44.66) * mm});
            skArc(sketch, "E79.13", {"start": v(-59.98, 45.37) * mm, "mid": v(-60, 45.02) * mm, "end": v(-60, 44.66) * mm});
            skArc(sketch, "E79.14", {"start": v(59.98, 45.37) * mm, "mid": v(0, 101.25) * mm, "end": v(-59.98, 45.37) * mm});
            skArc(sketch, "E79.15", {"start": v(60, 44.66) * mm, "mid": v(60, 45.02) * mm, "end": v(59.98, 45.37) * mm});
            skLineSegment(sketch, "E79.16", {"start": v(60, 44.66) * mm, "end": v(60, -44.66) * mm});
            skArc(sketch, "E79.17", {"start": v(59.98, -45.37) * mm, "mid": v(60, -45.02) * mm, "end": v(60, -44.66) * mm});
            skArc(sketch, "E79.18", {"start": v(-59.98, -45.37) * mm, "mid": v(0, -101.25) * mm, "end": v(59.98, -45.37) * mm});
            skArc(sketch, "E79.19", {"start": v(-60, -44.66) * mm, "mid": v(-60, -45.02) * mm, "end": v(-59.98, -45.37) * mm});
            skLineSegment(sketch, "E80", {"start": v(0, 135) * mm, "end": v(0, 165) * mm, "construction": true});
            skPoint(sketch, "E80.endSnap0", {"position": v(0, 135) * mm});
            skCircle(sketch, "E81", {"center": v(0, 165) * mm, "radius": 6 * mm});
            skLineSegment(sketch, "E82", {"start": v(-33, 135) * mm, "end": v(-15, 153) * mm});
            skLineSegment(sketch, "E83", {"start": v(-15, 153) * mm, "end": v(-15, 165) * mm});
            skLineSegment(sketch, "E84", {"start": v(33, 135) * mm, "end": v(15, 153) * mm});
            skLineSegment(sketch, "E85", {"start": v(15, 153) * mm, "end": v(15, 165) * mm});
            skArc(sketch, "E86", {"start": v(15, 165) * mm, "mid": v(0, 180) * mm, "end": v(-15, 165) * mm});
            skLineSegment(sketch, "E87", {"start": v(-80, 0) * mm, "end": v(80, 0) * mm, "construction": true});
            skLineSegment(sketch, "E88.MirrorCS", {"start": v(0, -135) * mm, "end": v(0, -165) * mm, "construction": true});
            skPoint(sketch, "E89.MirrorP", {"position": v(0, -135) * mm});
            skLineSegment(sketch, "E90.MirrorCS", {"start": v(-33, -135) * mm, "end": v(-15, -153) * mm});
            skLineSegment(sketch, "E91.MirrorCS", {"start": v(-15, -153) * mm, "end": v(-15, -165) * mm});
            skLineSegment(sketch, "E92.MirrorCS", {"start": v(33, -135) * mm, "end": v(15, -153) * mm});
            skArc(sketch, "E93.MirrorCS", {"start": v(15, -165) * mm, "mid": v(0, -180) * mm, "end": v(-15, -165) * mm});
            skLineSegment(sketch, "E94.MirrorCS", {"start": v(15, -153) * mm, "end": v(15, -165) * mm});
            skCircle(sketch, "E95.MirrorC", {"center": v(0, -165) * mm, "radius": 6 * mm});
            skSolve(sketch);
        }
        {
            var Q0;
            Q0 = qSketchRegion(id + "F16", true);
            var Q1;
            Q1=makeQuery(id+"F2.opExtrude","CAP_FACE",FACE,{"disambiguationData":[OSD([sQuery(id+"F0.wireOp",EDGE,"E12"),sQuery(id+"F0.wireOp",EDGE,"E13"),sQuery(id+"F0.wireOp",EDGE,"E14"),sQuery(id+"F0.wireOp",EDGE,"E15"),sQuery(id+"F0.wireOp",EDGE,"E17.filletArc"),sQuery(id+"F0.wireOp",EDGE,"E18.filletArc"),sQuery(id+"F0.wireOp",EDGE,"E19.filletArc"),sQuery(id+"F0.wireOp",EDGE,"E20.filletArc"),sQuery(id+"F0.wireOp",EDGE,"E25.0"),sQuery(id+"F0.wireOp",EDGE,"E25.1"),sQuery(id+"F0.wireOp",EDGE,"E25.2"),sQuery(id+"F0.wireOp",EDGE,"E25.3"),sQuery(id+"F0.wireOp",EDGE,"E25.4"),sQuery(id+"F0.wireOp",EDGE,"E25.5"),sQuery(id+"F0.wireOp",EDGE,"E25.6"),sQuery(id+"F0.wireOp",EDGE,"E25.7")])],"isStart":false});
            extrude(context, id + "F17", {"entities" : qUnion([Q0]), "operationType" : NewBodyOperationType.ADD, "endBound" : BoundingType.UP_TO_SURFACE, "endBoundEntityFace" : qUnion([Q1]), "depth" : 25 * mm});
        }
    });
